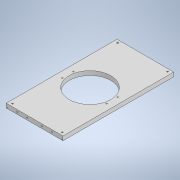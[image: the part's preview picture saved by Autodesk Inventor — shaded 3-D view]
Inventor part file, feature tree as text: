
AUTODESK INVENTOR PART (.ipt)
format: ipt  version: 2021.3 (Build 253353000, 353)  size: 176,640 bytes
history: native  units: mm
features: sketch x6, hole x4, extrude x2
ambient origin geometry x8: Origin, YZ Plane, XZ Plane, XY Plane, X Axis, Y Axis, Z Axis, Center Point
bodies: Body1 (feature_tree)
feature tree (12):
  extrude  "Extrusion1"  Depth=205.0mm
  hole  "Bohrung1"  [1 undecoded]
  sketch  "Skizze4"  dims[d13=180.0mm d14=380.0mm]
  hole  "Bohrung4"  [1 undecoded]
  hole  "Bohrung5"  [1 undecoded]
  extrude  "Extrusion2"  Depth=7.5mm
  hole  "Bohrung6"  [1 undecoded]
  sketch  "Skizze2"  dims[d8=150.0mm d9=205.0mm]
  sketch  "Skizze3"  dims[d10=400.0mm d11=15.0mm d12=0.0mm]
  sketch  "Skizze5"  dims[d15=4.917mm d16=20.0mm d17=4.0mm d18=2.0mm d19=90.0deg d20=8.0mm d21=20.594885mm d23=40.0mm]
  sketch  "Skizze6"  dims[d24=7.5mm d25=7.5mm]
  sketch  "Skizze7"  dims[d27=40.0mm d28=7.5mm d29=7.5mm d44=36.0mm d45=36.0mm d46=7.5mm d47=7.5mm d48=40.0mm d49=7.5mm d50=7.5mm d51=36.0mm d52=36.0mm d53=40.0mm d54=4.134mm d55=10.0mm d56=4.0mm d57=2.0mm d58=90.0deg d59=14.2mm d60=20.594885mm d61=4.134mm d62=10.0mm d63=4.0mm d64=2.0mm d65=90.0deg d66=14.2mm d67=20.594885mm d68=2.5mm d70=2.5mm d72=2.5mm d73=0.0mm d74=160.0mm d75=40.0mm d76=4.134mm d77=10.0mm d78=4.0mm d79=2.0mm d80=90.0deg d81=14.2mm d82=20.594885mm d84=198.0mm d85=99.0mm]
note: 4 required parameter values undecoded (feature->parameter linkage not recoverable at this tier; creation-order binding heuristic only, values carry confidence <= 0.55)
